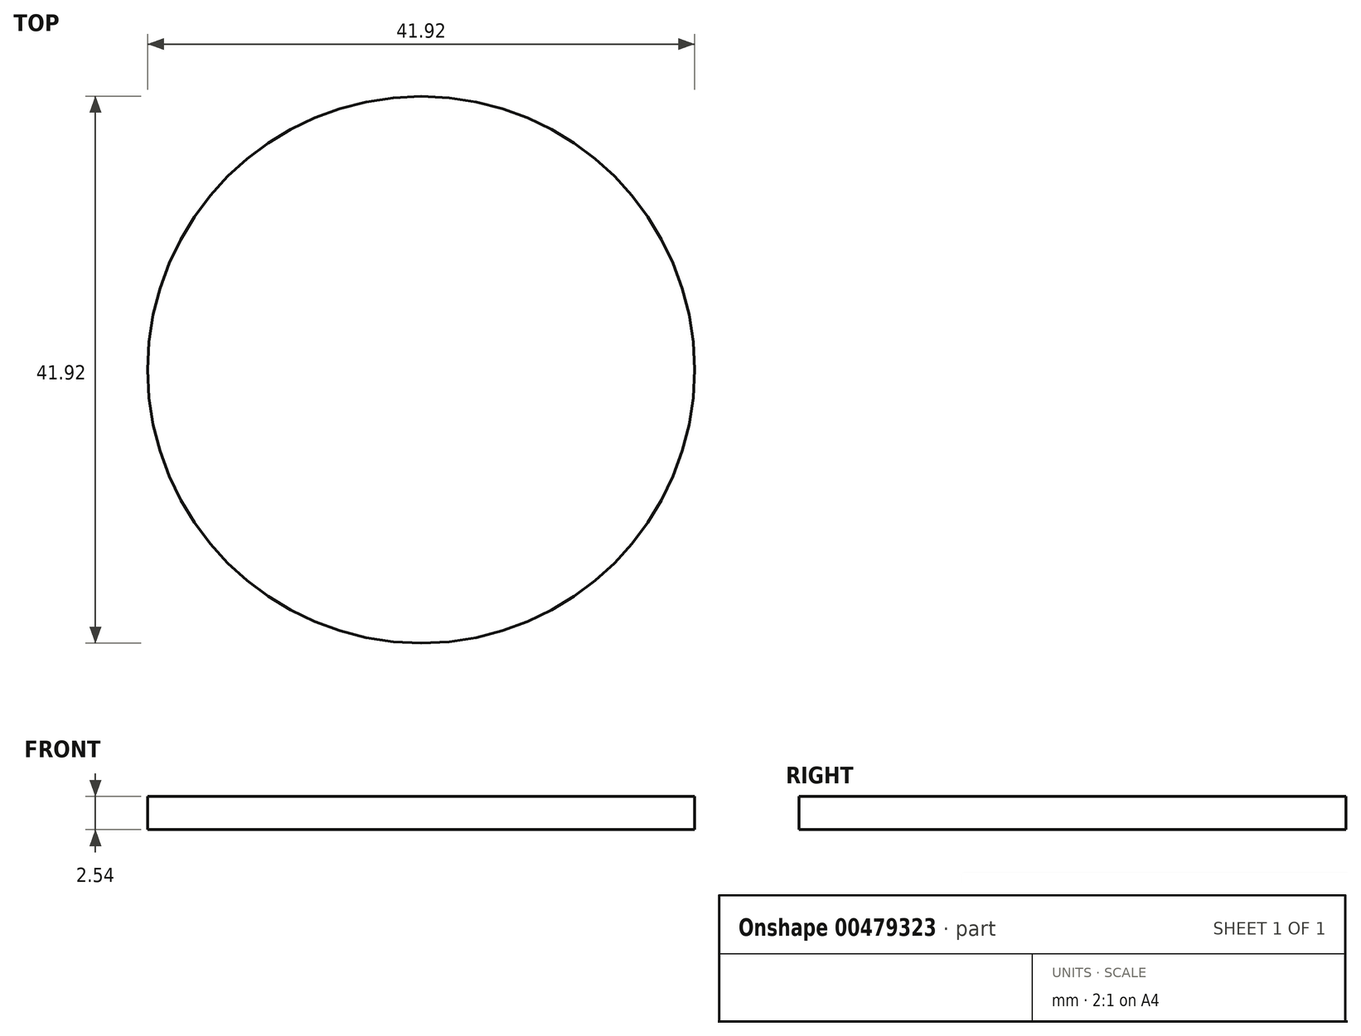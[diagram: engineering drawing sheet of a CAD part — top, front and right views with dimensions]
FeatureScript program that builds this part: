
annotation { "Feature Type Name" : "Feature", "Feature Type Description" : "" }
export const myFeature = defineFeature(function(context is Context, id is Id, definition is map)
    precondition{}
    {
        {
            var Q0;
            Q0=qCreatedBy(makeId("Top.planeOp"),FACE);
            var sketch = newSketch(context, id + "F0", { "sketchPlane" : qUnion([Q0])});
            skCircle(sketch, "E0", {"center": v(0, 0) * mm, "radius": 20.96 * mm});
            skSolve(sketch);
        }
        {
            var Q0;
            Q0=makeQuery(id+"F0.imprint","IMPRINT",FACE,{"disambiguationData":[TD([[makeQuery(id+"F0.imprint","IMPRINT",EDGE,{"derivedFrom":sQuery(id+"F0.wireOp",EDGE,"E0")}),1.0]])]});
            extrude(context, id + "F1", {"entities" : qUnion([Q0]), "depth" : 2.54 * mm, "offsetDistance" : 25.4 * mm});
        }
    });
